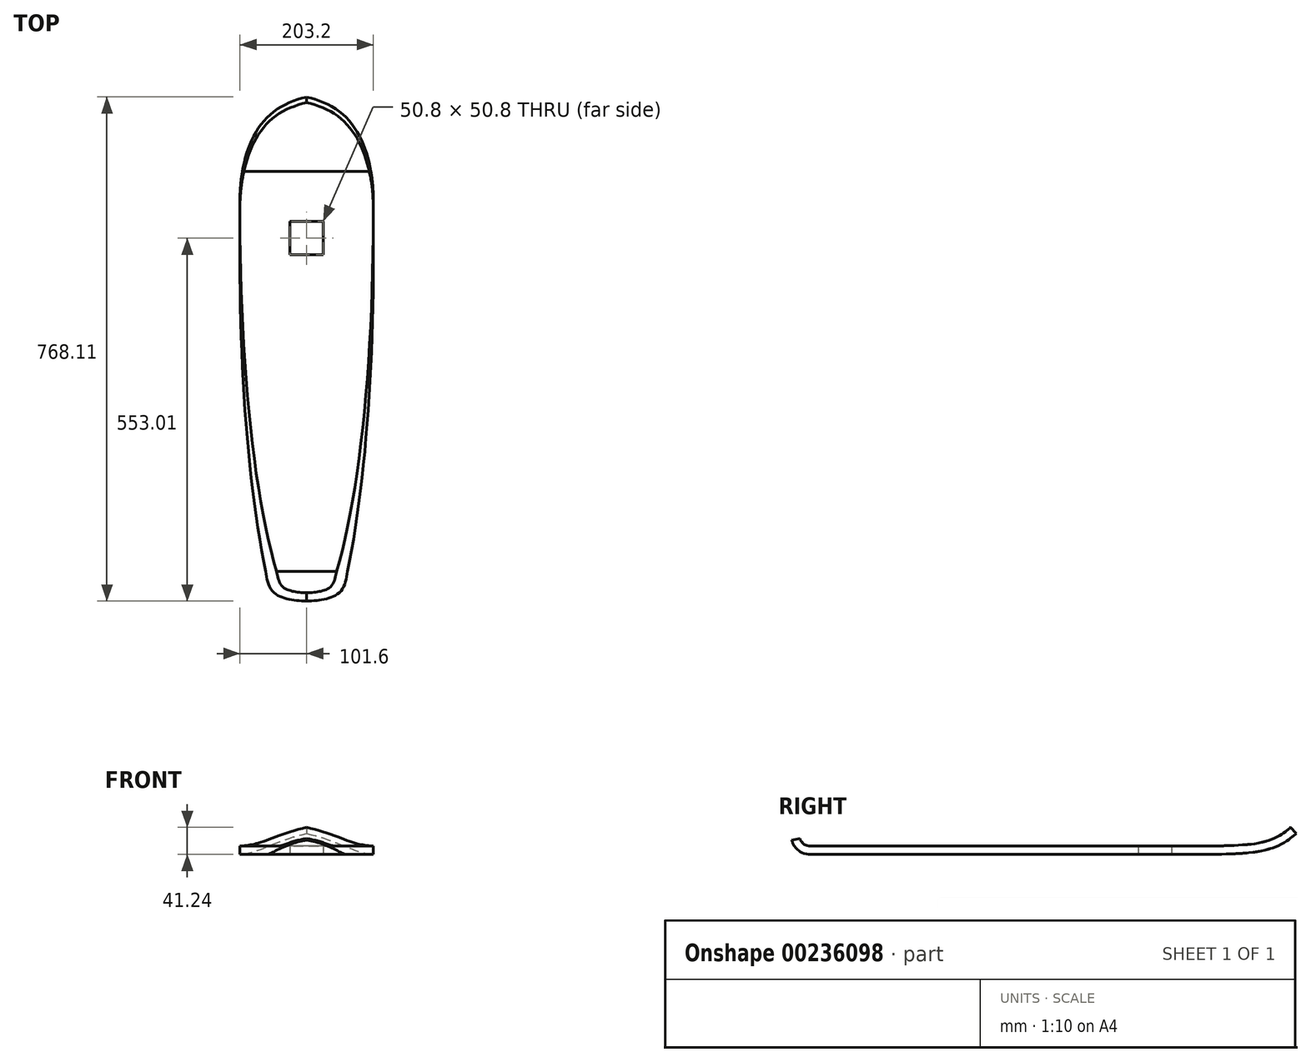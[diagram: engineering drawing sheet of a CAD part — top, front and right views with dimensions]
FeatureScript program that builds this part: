
annotation { "Feature Type Name" : "Feature", "Feature Type Description" : "" }
export const myFeature = defineFeature(function(context is Context, id is Id, definition is map)
    precondition{}
    {
        {
            var Q0;
            Q0=qCreatedBy(makeId("Top.planeOp"),FACE);
            var sketch = newSketch(context, id + "F0", { "sketchPlane" : qUnion([Q0])});
            skLineSegment(sketch, "E0.bottom", {"start": v(101.6, -304.8) * mm, "end": v(-101.6, -304.8) * mm});
            skLineSegment(sketch, "E0.top", {"start": v(101.6, 304.8) * mm, "end": v(-101.6, 304.8) * mm});
            skLineSegment(sketch, "E0.left", {"start": v(101.6, -304.8) * mm, "end": v(101.6, 304.8) * mm});
            skLineSegment(sketch, "E0.right", {"start": v(-101.6, -304.8) * mm, "end": v(-101.6, 304.8) * mm});
            skPoint(sketch, "E0.middle", {"position": v(0, 0) * mm});
            skLineSegment(sketch, "E1.bottom", {"start": v(25.4, 177.8) * mm, "end": v(-25.4, 177.8) * mm});
            skLineSegment(sketch, "E1.top", {"start": v(25.4, 228.6) * mm, "end": v(-25.4, 228.6) * mm});
            skLineSegment(sketch, "E1.left", {"start": v(25.4, 177.8) * mm, "end": v(25.4, 228.6) * mm});
            skLineSegment(sketch, "E1.right", {"start": v(-25.4, 177.8) * mm, "end": v(-25.4, 228.6) * mm});
            skPoint(sketch, "E1.middle", {"position": v(0, 203.2) * mm});
            skSolve(sketch);
        }
        {
            var Q0;
            Q0 = qSketchRegion(id + "F0", true);
            extrude(context, id + "F1", {"entities" : qUnion([Q0]), "endBound" : BoundingType.SYMMETRIC, "depth" : 12.7 * mm});
        }
        {
            var Q0;
            Q0=qCreatedBy(makeId("Right.planeOp"),FACE);
            var sketch = newSketch(context, id + "F2", { "sketchPlane" : qUnion([Q0])});
            skFitSpline(sketch, "E2", {"points": [v(306.17, 0) * mm, v(362.75, 4.52) * mm, v(396.7, 16.67) * mm, v(413.04, 28.82) * mm, v(419.74, 35.1) * mm], "startDerivative": vector(166.92, 5.32) * mm, "endDerivative": vector(41.9, 40.53) * mm});
            skSolve(sketch);
        }
        {
            var Q0;
            Q0=makeQuery(id+"F1.opExtrude","SWEPT_FACE",FACE,{"disambiguationData":[OSD([sQuery(id+"F0.wireOp",EDGE,"E0.top")])]});
            var Q1;
            Q1=sQuery(id+"F2.wireOp",EDGE,"E2");
            sweep(context, id + "F3", {"operationType" : NewBodyOperationType.ADD, "profiles" : qUnion([Q0]), "path" : qUnion([Q1])});
        }
        {
            var Q0;
            Q0=qCreatedBy(makeId("Right.planeOp"),FACE);
            var sketch = newSketch(context, id + "F4", { "sketchPlane" : qUnion([Q0])});
            skPoint(sketch, "E3.0.internal.orphan", {"position": v(-304.68, 0) * mm});
            skFitSpline(sketch, "E4", {"points": [v(-304.68, 0) * mm, v(-332.15, 2.1) * mm, v(-341.91, 11.86) * mm, v(-343.91, 17.61) * mm], "startDerivative": vector(-67.2, -3.69) * mm, "endDerivative": vector(-6.17, 24.8) * mm});
            skFitSpline(sketch, "E5", {"points": [v(-343.91, 17.61) * mm, v(-346.42, 23.22) * mm, v(-349.3, 32.75) * mm], "startDerivative": vector(-5.82, 11.8) * mm, "endDerivative": vector(-4.99, 18.21) * mm});
            skSolve(sketch);
        }
        {
            var Q0;
            Q0=makeQuery(id+"F1.opExtrude","SWEPT_FACE",FACE,{"disambiguationData":[OSD([sQuery(id+"F0.wireOp",EDGE,"E0.bottom")])]});
            var Q1;
            Q1=sQuery(id+"F4.wireOp",EDGE,"E4");
            sweep(context, id + "F5", {"operationType" : NewBodyOperationType.ADD, "profiles" : qUnion([Q0]), "path" : qUnion([Q1])});
        }
        {
            var Q0;
            Q0=makeQuery(id+"F5.opSweep","CAP_EDGE",EDGE,{"disambiguationData":[OSD([sQuery(id+"F0.wireOp",EDGE,"E0.bottom"),sQuery(id+"F0.wireOp",EDGE,"E0.left"),sQuery(id+"F4.wireOp",VERTEX,"E4.end")])],"isStart":false});
            var Q1;
            Q1=makeQuery(id+"F5.opSweep","CAP_EDGE",EDGE,{"disambiguationData":[OSD([sQuery(id+"F0.wireOp",EDGE,"E0.bottom"),sQuery(id+"F0.wireOp",EDGE,"E0.right"),sQuery(id+"F4.wireOp",VERTEX,"E4.end")])],"isStart":false});
            fillet(context, id + "F6", {"entities" : qUnion([Q0, Q1]), "radius" : 119.58 * mm, "tangentPropagation" : true, "allowEdgeOverflow" : false});
        }
        {
            var Q0;
            Q0=makeQuery(id+"F3.opSweep","CAP_EDGE",EDGE,{"disambiguationData":[OSD([sQuery(id+"F0.wireOp",EDGE,"E0.top"),sQuery(id+"F0.wireOp",EDGE,"E0.left"),sQuery(id+"F2.wireOp",VERTEX,"E2.end")])],"isStart":false});
            var Q1;
            Q1=makeQuery(id+"F3.opSweep","CAP_EDGE",EDGE,{"disambiguationData":[OSD([sQuery(id+"F0.wireOp",EDGE,"E0.top"),sQuery(id+"F0.wireOp",EDGE,"E0.right"),sQuery(id+"F2.wireOp",VERTEX,"E2.end")])],"isStart":false});
            var Q2;
            Q2=makeQuery(id+"F6.opFillet","BLEND_EDGE",EDGE,{"blendedFrom":[makeQuery(id+"F5.opSweep","CAP_EDGE",EDGE,{"disambiguationData":[OSD([sQuery(id+"F0.wireOp",EDGE,"E0.bottom"),sQuery(id+"F0.wireOp",EDGE,"E0.left"),sQuery(id+"F4.wireOp",VERTEX,"E4.end")])],"isStart":false}),makeQuery(id+"F3.opSweep","CAP_FACE",FACE,{"disambiguationData":[OSD([sQuery(id+"F0.wireOp",EDGE,"E0.top"),sQuery(id+"F2.wireOp",VERTEX,"E2.end")])],"isStart":false})],"blendedInto":[makeQuery(id+"F3.opSweep","CAP_FACE",FACE,{"disambiguationData":[OSD([sQuery(id+"F0.wireOp",EDGE,"E0.top"),sQuery(id+"F2.wireOp",VERTEX,"E2.end")])],"isStart":false})]});
            var Q3;
            Q3=makeQuery(id+"F6.opFillet","BLEND_EDGE",EDGE,{"blendedFrom":[makeQuery(id+"F5.opSweep","CAP_EDGE",EDGE,{"disambiguationData":[OSD([sQuery(id+"F0.wireOp",EDGE,"E0.bottom"),sQuery(id+"F0.wireOp",EDGE,"E0.right"),sQuery(id+"F4.wireOp",VERTEX,"E4.end")])],"isStart":false}),makeQuery(id+"F3.opSweep","CAP_FACE",FACE,{"disambiguationData":[OSD([sQuery(id+"F0.wireOp",EDGE,"E0.top"),sQuery(id+"F2.wireOp",VERTEX,"E2.end")])],"isStart":false})],"blendedInto":[makeQuery(id+"F3.opSweep","CAP_FACE",FACE,{"disambiguationData":[OSD([sQuery(id+"F0.wireOp",EDGE,"E0.top"),sQuery(id+"F2.wireOp",VERTEX,"E2.end")])],"isStart":false})]});
            fillet(context, id + "F7", {"entities" : qUnion([Q0, Q1, Q2, Q3]), "radius" : 144.24 * mm, "tangentPropagation" : true, "allowEdgeOverflow" : false});
        }
    });
